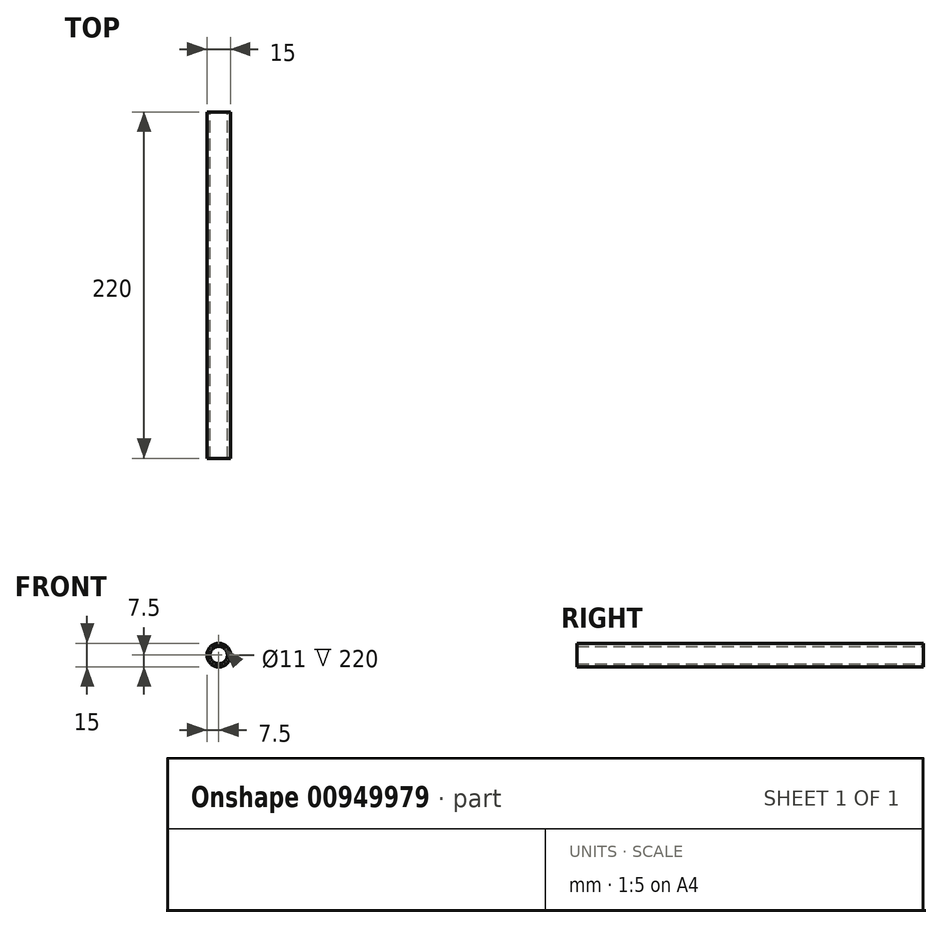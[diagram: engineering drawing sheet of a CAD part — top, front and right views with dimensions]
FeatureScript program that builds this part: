
annotation { "Feature Type Name" : "Feature", "Feature Type Description" : "" }
export const myFeature = defineFeature(function(context is Context, id is Id, definition is map)
    precondition{}
    {
        {
            var Q0;
            Q0=qCreatedBy(makeId("Front.planeOp"),FACE);
            var sketch = newSketch(context, id + "F0", { "sketchPlane" : qUnion([Q0])});
            skCircle(sketch, "E0", {"center": v(0, 0) * mm, "radius": 7.5 * mm});
            skCircle(sketch, "E1", {"center": v(0, 0) * mm, "radius": 5.5 * mm});
            skSolve(sketch);
        }
        {
            var Q0;
            Q0=makeQuery(id+"F0.imprint","IMPRINT",FACE,{"disambiguationData":[TD([[makeQuery(id+"F0.imprint","IMPRINT",EDGE,{"derivedFrom":sQuery(id+"F0.wireOp",EDGE,"E0")}),1.0]])]});
            extrude(context, id + "F1", {"entities" : qUnion([Q0]), "depth" : 220 * mm, "offsetDistance" : 25 * mm});
        }
    });
